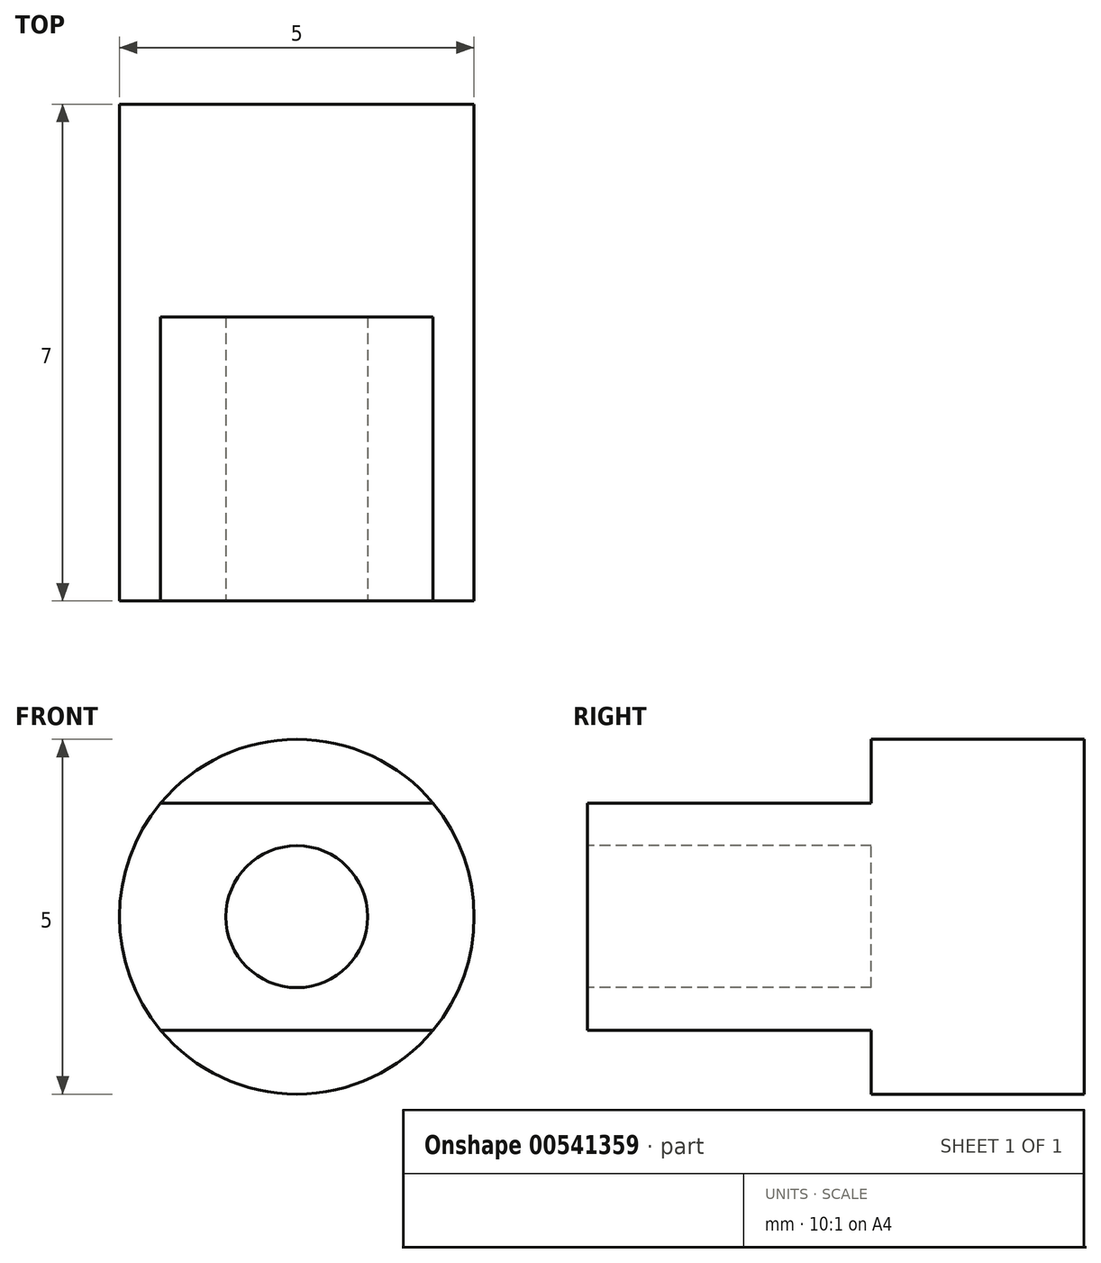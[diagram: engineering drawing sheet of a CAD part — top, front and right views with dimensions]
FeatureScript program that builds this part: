
annotation { "Feature Type Name" : "Feature", "Feature Type Description" : "" }
export const myFeature = defineFeature(function(context is Context, id is Id, definition is map)
    precondition{}
    {
        {
            var Q0;
            Q0=qCreatedBy(makeId("Front.planeOp"),FACE);
            var sketch = newSketch(context, id + "F0", { "sketchPlane" : qUnion([Q0])});
            skCircle(sketch, "E0", {"center": v(0, 0) * mm, "radius": 2.5 * mm});
            skSolve(sketch);
        }
        {
            var Q0;
            Q0=makeQuery(id+"F0.imprint","IMPRINT",FACE,{"disambiguationData":[TD([[makeQuery(id+"F0.imprint","IMPRINT",EDGE,{"derivedFrom":sQuery(id+"F0.wireOp",EDGE,"E0")}),1.0]])]});
            extrude(context, id + "F1", {"entities" : qUnion([Q0]), "depth" : 3 * mm, "offsetDistance" : 25 * mm});
        }
        {
            var Q0;
            Q0=makeQuery(id+"F1.opExtrude","CAP_FACE",FACE,{"disambiguationData":[OSD([sQuery(id+"F0.wireOp",EDGE,"E0")])],"isStart":false});
            var sketch = newSketch(context, id + "F2", { "sketchPlane" : qUnion([Q0])});
            skArc(sketch, "E1.0", {"start": v(-1.92, 1.6) * mm, "mid": v(-2.5, 0) * mm, "end": v(-1.92, -1.6) * mm});
            skLineSegment(sketch, "E2", {"start": v(-1.92, 1.6) * mm, "end": v(1.92, 1.6) * mm});
            skLineSegment(sketch, "E3", {"start": v(-1.92, -1.6) * mm, "end": v(1.92, -1.6) * mm});
            skArc(sketch, "E4.trimOffspring", {"start": v(1.92, -1.6) * mm, "mid": v(2.5, 0) * mm, "end": v(1.92, 1.6) * mm});
            skSolve(sketch);
        }
        {
            var Q0;
            Q0=makeQuery(id+"F2.imprint","IMPRINT",FACE,{"disambiguationData":[TD([[makeQuery(id+"F2.imprint","IMPRINT",EDGE,{"derivedFrom":sQuery(id+"F2.wireOp",EDGE,"E1.0")}),1.0]])]});
            extrude(context, id + "F3", {"entities" : qUnion([Q0]), "operationType" : NewBodyOperationType.ADD, "depth" : 4 * mm, "offsetDistance" : 25 * mm});
        }
        {
            var Q0;
            Q0=makeQuery(id+"F3.opExtrude","CAP_FACE",FACE,{"disambiguationData":[OSD([sQuery(id+"F2.wireOp",EDGE,"E1.0"),sQuery(id+"F2.wireOp",EDGE,"E2"),sQuery(id+"F2.wireOp",EDGE,"E3"),sQuery(id+"F2.wireOp",EDGE,"E4.trimOffspring")])],"isStart":false});
            var sketch = newSketch(context, id + "F4", { "sketchPlane" : qUnion([Q0])});
            skCircle(sketch, "E5", {"center": v(0, 0) * mm, "radius": 1 * mm});
            skSolve(sketch);
        }
        {
            var Q0;
            Q0=makeQuery(id+"F4.imprint","IMPRINT",FACE,{"disambiguationData":[TD([[makeQuery(id+"F4.imprint","IMPRINT",EDGE,{"derivedFrom":sQuery(id+"F4.wireOp",EDGE,"E5")}),1.0]])]});
            extrude(context, id + "F5", {"entities" : qUnion([Q0]), "operationType" : NewBodyOperationType.REMOVE, "oppositeDirection" : true, "depth" : 4 * mm, "offsetDistance" : 25 * mm});
        }
    });
